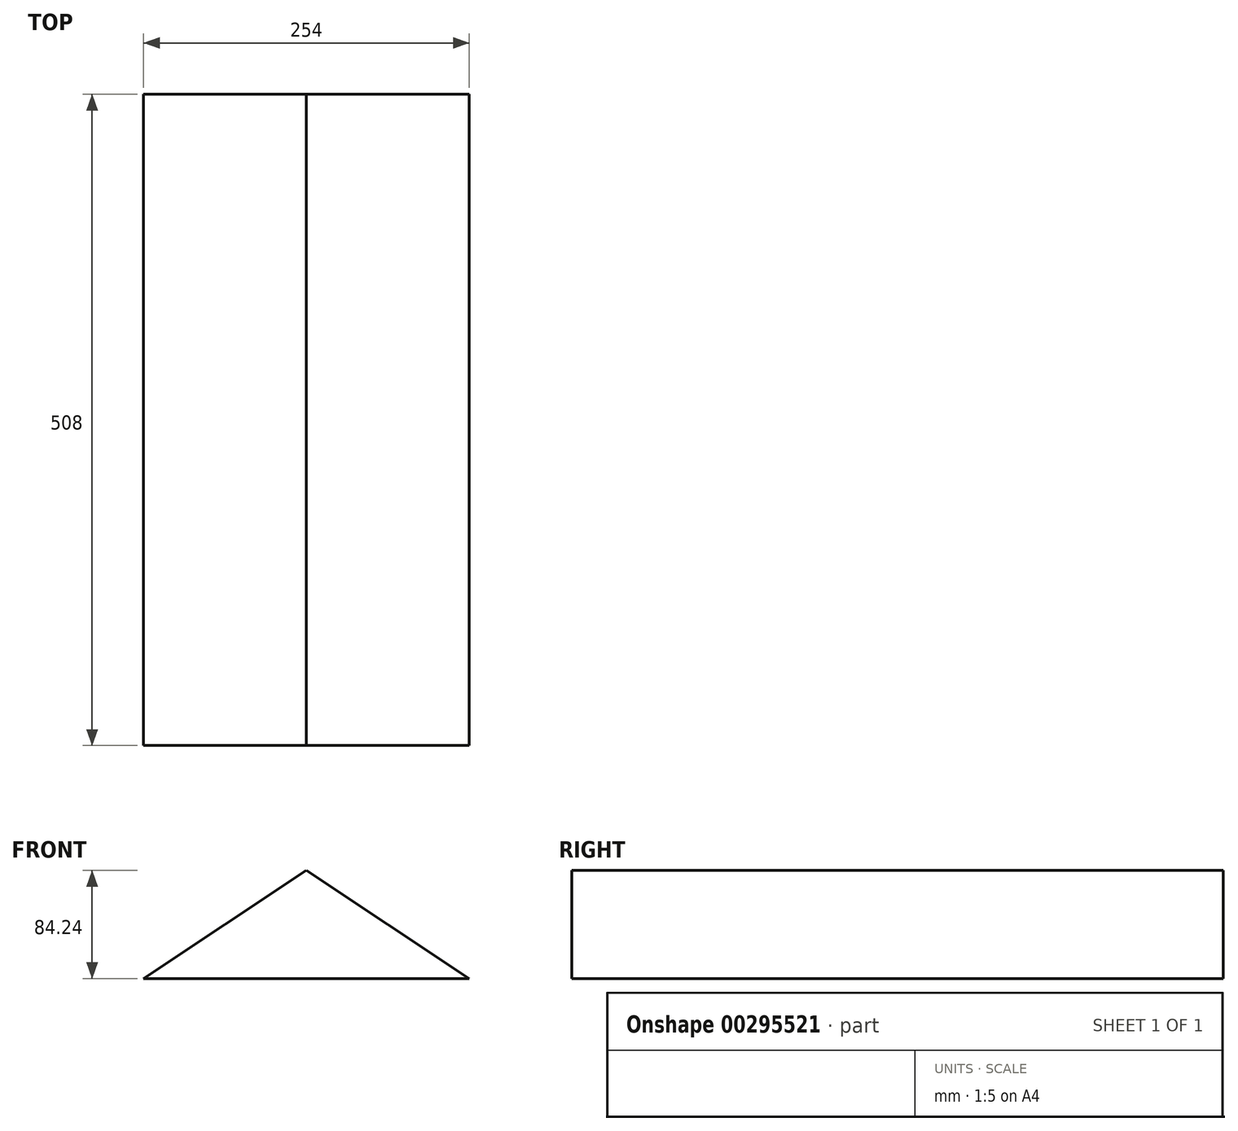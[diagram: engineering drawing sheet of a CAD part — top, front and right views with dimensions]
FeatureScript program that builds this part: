
annotation { "Feature Type Name" : "Feature", "Feature Type Description" : "" }
export const myFeature = defineFeature(function(context is Context, id is Id, definition is map)
    precondition{}
    {
        {
            var Q0;
            Q0=qCreatedBy(makeId("Front.planeOp"),FACE);
            var sketch = newSketch(context, id + "F0", { "sketchPlane" : qUnion([Q0])});
            skLineSegment(sketch, "E0", {"start": v(0, 0) * mm, "end": v(254, 0) * mm});
            skLineSegment(sketch, "E1", {"start": v(254, 0) * mm, "end": v(127, 84.24) * mm});
            skLineSegment(sketch, "E2", {"start": v(0, 0) * mm, "end": v(127, 84.24) * mm});
            skSolve(sketch);
        }
        {
            var Q0;
            Q0=makeQuery(id+"F0.imprint","IMPRINT",FACE,{"disambiguationData":[TD([[makeQuery(id+"F0.imprint","IMPRINT",EDGE,{"derivedFrom":sQuery(id+"F0.wireOp",EDGE,"E0")}),1.0]])]});
            extrude(context, id + "F1", {"entities" : qUnion([Q0]), "depth" : 508 * mm});
        }
    });
